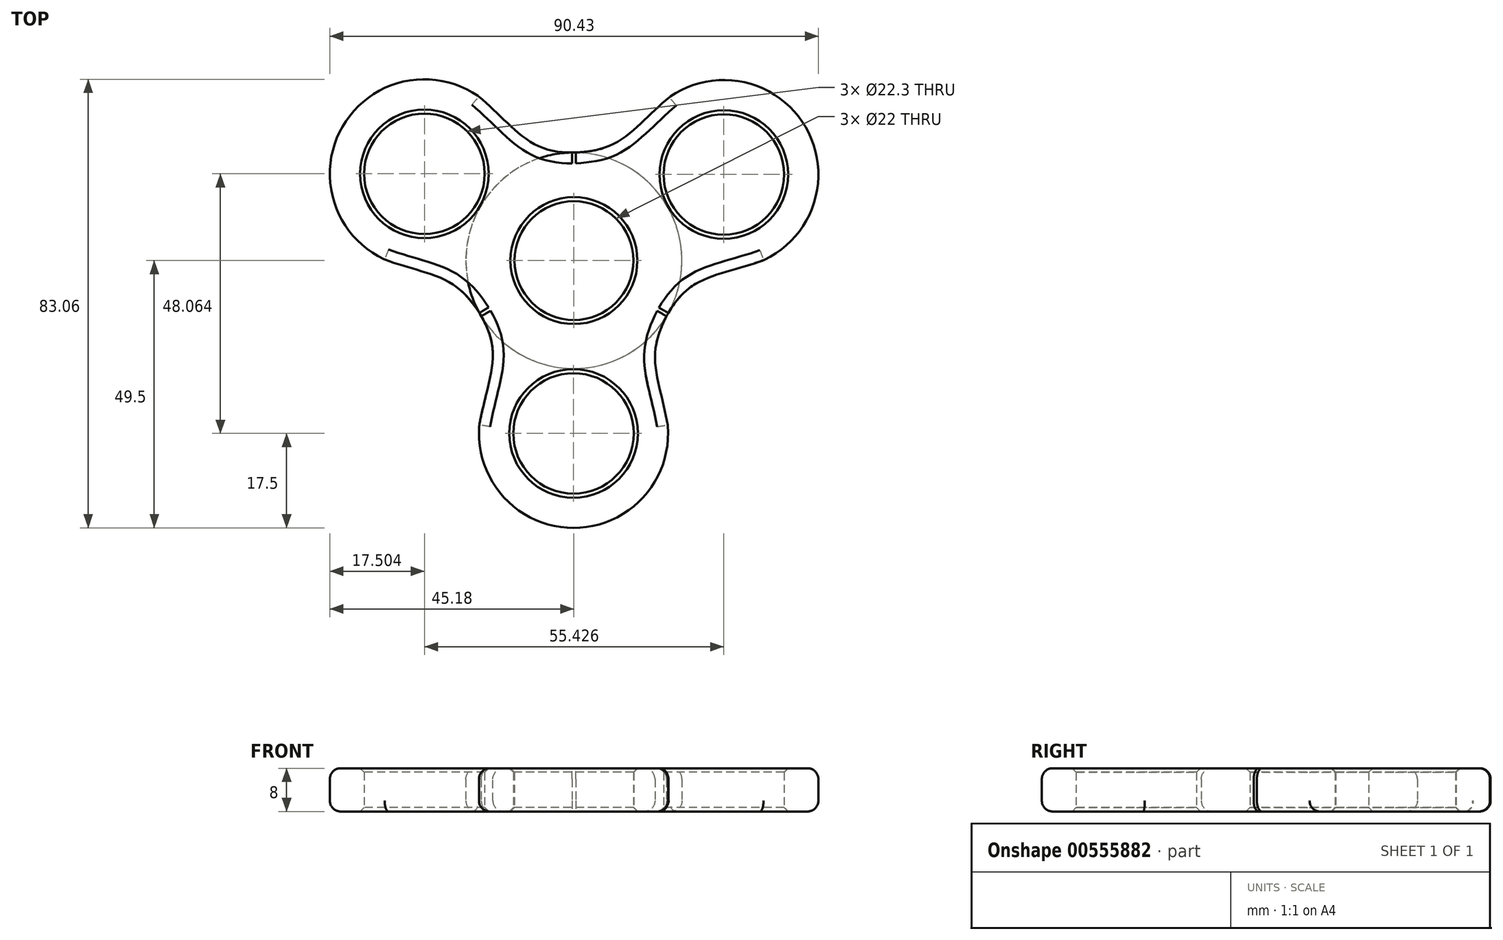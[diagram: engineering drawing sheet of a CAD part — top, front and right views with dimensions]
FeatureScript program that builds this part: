
annotation { "Feature Type Name" : "Feature", "Feature Type Description" : "" }
export const myFeature = defineFeature(function(context is Context, id is Id, definition is map)
    precondition{}
    {
        {
            var Q0;
            Q0=qCreatedBy(makeId("Top.planeOp"),FACE);
            var sketch = newSketch(context, id + "F0", { "sketchPlane" : qUnion([Q0])});
            skCircle(sketch, "E0.MirrorC", {"center": v(0, 0) * mm, "radius": 11 * mm});
            skCircle(sketch, "E1", {"center": v(-0.07, -32) * mm, "radius": 11.15 * mm});
            skLineSegment(sketch, "E2", {"start": v(0, 0) * mm, "end": v(-0.12, 20) * mm});
            skArc(sketch, "E3", {"start": v(17.15, -10.3) * mm, "mid": v(0, 20) * mm, "end": v(-17.15, -10.3) * mm});
            skFitSpline(sketch, "E4", {"points": [v(-17.51, -30.52) * mm, v(-15, -17.68) * mm, v(-17.15, -10.3) * mm], "startDerivative": vector(4.17, 24.17) * mm, "endDerivative": vector(-9.07, 15.88) * mm});
            skFitSpline(sketch, "E5", {"points": [v(17.15, -10.3) * mm, v(15, -17.68) * mm, v(17.36, -30.52) * mm], "startDerivative": vector(-7.03, -14) * mm, "endDerivative": vector(3.84, -24.18) * mm});
            skArc(sketch, "E6", {"start": v(-17.51, -30.52) * mm, "mid": v(-0.07, -49.5) * mm, "end": v(17.36, -30.52) * mm});
            skSolve(sketch);
        }
        {
            var Q0;
            Q0 = qSketchRegion(id + "F0", true);
            extrude(context, id + "F1", {"entities" : qUnion([Q0]), "depth" : 8 * mm, "offsetDistance" : 25 * mm});
        }
        {
            var Q0;
            Q0=qCreatedBy(makeId("Front.planeOp"),FACE);
            var sketch = newSketch(context, id + "F2", { "sketchPlane" : qUnion([Q0])});
            skLineSegment(sketch, "E7", {"start": v(0, 0) * mm, "end": v(0, 36.14) * mm});
            skSolve(sketch);
        }
        {
            var Q0;
            Q0=makeQuery(id+"F1.opExtrude","SWEPT_BODY",BODY,{"disambiguationData":[OSD([sQuery(id+"F0.wireOp",EDGE,"f3960193-eab3-4b8b-a0f2-21ab98192fe2"),sQuery(id+"F0.wireOp",EDGE,"da26f408-d12f-4fae-93dc-3efbcd1e3af21.MirrorC"),sQuery(id+"F0.wireOp",EDGE,"14506032-b490-4246-af5a-1439987a0185.MirrorC"),sQuery(id+"F0.wireOp",EDGE,"61171388-bded-4786-97b8-63b4edcb6984.MirrorC"),sQuery(id+"F0.wireOp",EDGE,"9475da3a-7f2b-4840-8aec-7bdfa3fc84fe.MirrorC"),sQuery(id+"F0.wireOp",EDGE,"f5e62fb9-18b1-4003-8d50-6765dd313fea"),sQuery(id+"F0.wireOp",EDGE,"e2af428d-a368-4ff8-af57-03d4f12e0fbb")])]});
            var Q1;
            Q1=makeQuery(id+"F1.opExtrude","SWEPT_BODY",BODY,{"disambiguationData":[OSD([sQuery(id+"F0.wireOp",EDGE,"E0.MirrorC"),sQuery(id+"F0.wireOp",EDGE,"E1"),sQuery(id+"F0.wireOp",EDGE,"E3"),sQuery(id+"F0.wireOp",EDGE,"E4"),sQuery(id+"F0.wireOp",EDGE,"E5"),sQuery(id+"F0.wireOp",EDGE,"E6")])]});
            var Q2;
            Q2=sQuery(id+"F2.wireOp",EDGE,"E7");
            circularPattern(context, id + "F3", {"entities" : qUnion([Q0, Q1]), "axis" : qUnion([Q2]), "angle" : 360 * degree, "instanceCount" : 3, "equalSpace" : true});
        }
        {
            var Q0;
            Q0=makeQuery(id+"F3.opPattern","COPY",EDGE,{"derivedFrom":makeQuery(id+"F1.opExtrude","CAP_EDGE",EDGE,{"disambiguationData":[OSD([sQuery(id+"F0.wireOp",EDGE,"E1")])],"isStart":false}),"instanceName":"1"});
            var Q1;
            Q1=makeQuery(id+"F3.opPattern","COPY",EDGE,{"derivedFrom":makeQuery(id+"F1.opExtrude","CAP_EDGE",EDGE,{"disambiguationData":[OSD([sQuery(id+"F0.wireOp",EDGE,"E1")])],"isStart":true}),"instanceName":"1"});
            var Q2;
            Q2=makeQuery(id+"F1.opExtrude","CAP_EDGE",EDGE,{"disambiguationData":[OSD([sQuery(id+"F0.wireOp",EDGE,"E1")])],"isStart":false});
            var Q3;
            Q3=makeQuery(id+"F1.opExtrude","CAP_EDGE",EDGE,{"disambiguationData":[OSD([sQuery(id+"F0.wireOp",EDGE,"E1")])],"isStart":true});
            var Q4;
            Q4=makeQuery(id+"F3.opPattern","COPY",EDGE,{"derivedFrom":makeQuery(id+"F1.opExtrude","CAP_EDGE",EDGE,{"disambiguationData":[OSD([sQuery(id+"F0.wireOp",EDGE,"E1")])],"isStart":false}),"instanceName":"2"});
            var Q5;
            Q5=makeQuery(id+"F3.opPattern","COPY",EDGE,{"derivedFrom":makeQuery(id+"F1.opExtrude","CAP_EDGE",EDGE,{"disambiguationData":[OSD([sQuery(id+"F0.wireOp",EDGE,"E1")])],"isStart":true}),"instanceName":"2"});
            var Q6;
            Q6=makeQuery(id+"F3.opPattern","COPY",EDGE,{"derivedFrom":makeQuery(id+"F1.opExtrude","CAP_EDGE",EDGE,{"disambiguationData":[OSD([sQuery(id+"F0.wireOp",EDGE,"61171388-bded-4786-97b8-63b4edcb6984.MirrorC")])],"isStart":false}),"instanceName":"2"});
            var Q7;
            Q7=makeQuery(id+"F3.opPattern","COPY",EDGE,{"derivedFrom":makeQuery(id+"F1.opExtrude","CAP_EDGE",EDGE,{"disambiguationData":[OSD([sQuery(id+"F0.wireOp",EDGE,"61171388-bded-4786-97b8-63b4edcb6984.MirrorC")])],"isStart":true}),"instanceName":"2"});
            var Q8;
            Q8=makeQuery(id+"F3.opPattern","COPY",EDGE,{"derivedFrom":makeQuery(id+"F1.opExtrude","CAP_EDGE",EDGE,{"disambiguationData":[OSD([sQuery(id+"F0.wireOp",EDGE,"E0.MirrorC")])],"isStart":false}),"instanceName":"2"});
            var Q9;
            Q9=makeQuery(id+"F3.opPattern","COPY",EDGE,{"derivedFrom":makeQuery(id+"F1.opExtrude","CAP_EDGE",EDGE,{"disambiguationData":[OSD([sQuery(id+"F0.wireOp",EDGE,"E0.MirrorC")])],"isStart":true}),"instanceName":"2"});
            chamfer(context, id + "F4", {"entities" : qUnion([Q0, Q1, Q2, Q3, Q4, Q5, Q6, Q7, Q8, Q9]), "width" : .75 * mm, "tangentPropagation" : true});
        }
        {
            var Q0;
            Q0=makeQuery(id+"F3.opPattern","COPY",EDGE,{"derivedFrom":makeQuery(id+"F1.opExtrude","CAP_EDGE",EDGE,{"disambiguationData":[OSD([sQuery(id+"F0.wireOp",EDGE,"E5")])],"isStart":false}),"instanceName":"2"});
            var Q1;
            Q1=makeQuery(id+"F3.opPattern","COPY",EDGE,{"derivedFrom":makeQuery(id+"F1.opExtrude","CAP_EDGE",EDGE,{"disambiguationData":[OSD([sQuery(id+"F0.wireOp",EDGE,"E6")])],"isStart":false}),"instanceName":"2"});
            var Q2;
            Q2=makeQuery(id+"F3.opPattern","COPY",EDGE,{"derivedFrom":makeQuery(id+"F1.opExtrude","CAP_EDGE",EDGE,{"disambiguationData":[OSD([sQuery(id+"F0.wireOp",EDGE,"E4")])],"isStart":false}),"instanceName":"2"});
            var Q3;
            Q3=makeQuery(id+"F1.opExtrude","CAP_EDGE",EDGE,{"disambiguationData":[OSD([sQuery(id+"F0.wireOp",EDGE,"E4")])],"isStart":false});
            var Q4;
            Q4=makeQuery(id+"F1.opExtrude","CAP_EDGE",EDGE,{"disambiguationData":[OSD([sQuery(id+"F0.wireOp",EDGE,"E6")])],"isStart":false});
            var Q5;
            Q5=makeQuery(id+"F1.opExtrude","CAP_EDGE",EDGE,{"disambiguationData":[OSD([sQuery(id+"F0.wireOp",EDGE,"E5")])],"isStart":false});
            var Q6;
            Q6=makeQuery(id+"F3.opPattern","COPY",EDGE,{"derivedFrom":makeQuery(id+"F1.opExtrude","CAP_EDGE",EDGE,{"disambiguationData":[OSD([sQuery(id+"F0.wireOp",EDGE,"E5")])],"isStart":false}),"instanceName":"1"});
            var Q7;
            Q7=makeQuery(id+"F3.opPattern","COPY",EDGE,{"derivedFrom":makeQuery(id+"F1.opExtrude","CAP_EDGE",EDGE,{"disambiguationData":[OSD([sQuery(id+"F0.wireOp",EDGE,"E6")])],"isStart":false}),"instanceName":"1"});
            var Q8;
            Q8=makeQuery(id+"F3.opPattern","COPY",EDGE,{"derivedFrom":makeQuery(id+"F1.opExtrude","CAP_EDGE",EDGE,{"disambiguationData":[OSD([sQuery(id+"F0.wireOp",EDGE,"E4")])],"isStart":false}),"instanceName":"1"});
            var Q9;
            Q9=makeQuery(id+"F3.opPattern","COPY",EDGE,{"derivedFrom":makeQuery(id+"F1.opExtrude","CAP_EDGE",EDGE,{"disambiguationData":[OSD([sQuery(id+"F0.wireOp",EDGE,"E3")])],"isStart":false}),"instanceName":"1"});
            var Q10;
            Q10=makeQuery(id+"F3.opPattern","COPY",EDGE,{"derivedFrom":makeQuery(id+"F1.opExtrude","CAP_EDGE",EDGE,{"disambiguationData":[OSD([sQuery(id+"F0.wireOp",EDGE,"E3")])],"isStart":false}),"instanceName":"2"});
            var Q11;
            Q11=makeQuery(id+"F3.opPattern","COPY",EDGE,{"derivedFrom":makeQuery(id+"F1.opExtrude","CAP_EDGE",EDGE,{"disambiguationData":[OSD([sQuery(id+"F0.wireOp",EDGE,"E3")])],"isStart":true}),"instanceName":"2"});
            var Q12;
            Q12=makeQuery(id+"F3.opPattern","COPY",EDGE,{"derivedFrom":makeQuery(id+"F1.opExtrude","CAP_EDGE",EDGE,{"disambiguationData":[OSD([sQuery(id+"F0.wireOp",EDGE,"E3")])],"isStart":true}),"instanceName":"1"});
            var Q13;
            Q13=makeQuery(id+"F1.opExtrude","CAP_EDGE",EDGE,{"disambiguationData":[OSD([sQuery(id+"F0.wireOp",EDGE,"E3")])],"isStart":true});
            var Q14;
            Q14=makeQuery(id+"F1.opExtrude","CAP_EDGE",EDGE,{"disambiguationData":[OSD([sQuery(id+"F0.wireOp",EDGE,"E3")])],"isStart":false});
            fillet(context, id + "F5", {"entities" : qUnion([Q0, Q1, Q2, Q3, Q4, Q5, Q6, Q7, Q8, Q9, Q10, Q11, Q12, Q13, Q14]), "radius" : 2 * mm, "tangentPropagation" : true, "allowEdgeOverflow" : false});
        }
        {
            var Q0;
            Q0=makeQuery(id+"F3.opPattern","COPY",EDGE,{"derivedFrom":makeQuery(id+"F1.opExtrude","CAP_EDGE",EDGE,{"disambiguationData":[OSD([sQuery(id+"F0.wireOp",EDGE,"E0.MirrorC")])],"isStart":false}),"instanceName":"1"});
            var Q1;
            Q1=makeQuery(id+"F3.opPattern","COPY",EDGE,{"derivedFrom":makeQuery(id+"F1.opExtrude","CAP_EDGE",EDGE,{"disambiguationData":[OSD([sQuery(id+"F0.wireOp",EDGE,"E0.MirrorC")])],"isStart":true}),"instanceName":"1"});
            chamfer(context, id + "F6", {"entities" : qUnion([Q0, Q1]), "width" : .75 * mm, "tangentPropagation" : true});
        }
        {
            var Q0;
            Q0=makeQuery(id+"F1.opExtrude","CAP_EDGE",EDGE,{"disambiguationData":[OSD([sQuery(id+"F0.wireOp",EDGE,"E0.MirrorC")])],"isStart":false});
            var Q1;
            Q1=makeQuery(id+"F1.opExtrude","CAP_EDGE",EDGE,{"disambiguationData":[OSD([sQuery(id+"F0.wireOp",EDGE,"E0.MirrorC")])],"isStart":true});
            chamfer(context, id + "F7", {"entities" : qUnion([Q0, Q1]), "width" : .75 * mm, "tangentPropagation" : true});
        }
        {
            var Q0;
            Q0=makeQuery(id+"F3.opPattern","COPY",EDGE,{"derivedFrom":makeQuery(id+"F1.opExtrude","CAP_EDGE",EDGE,{"disambiguationData":[OSD([sQuery(id+"F0.wireOp",EDGE,"E4")])],"isStart":true}),"instanceName":"1"});
            var Q1;
            Q1=makeQuery(id+"F1.opExtrude","CAP_EDGE",EDGE,{"disambiguationData":[OSD([sQuery(id+"F0.wireOp",EDGE,"E5")])],"isStart":true});
            var Q2;
            Q2=makeQuery(id+"F1.opExtrude","CAP_EDGE",EDGE,{"disambiguationData":[OSD([sQuery(id+"F0.wireOp",EDGE,"E6")])],"isStart":true});
            var Q3;
            Q3=makeQuery(id+"F1.opExtrude","CAP_EDGE",EDGE,{"disambiguationData":[OSD([sQuery(id+"F0.wireOp",EDGE,"E4")])],"isStart":true});
            var Q4;
            Q4=makeQuery(id+"F3.opPattern","COPY",EDGE,{"derivedFrom":makeQuery(id+"F1.opExtrude","CAP_EDGE",EDGE,{"disambiguationData":[OSD([sQuery(id+"F0.wireOp",EDGE,"E5")])],"isStart":true}),"instanceName":"2"});
            var Q5;
            Q5=makeQuery(id+"F3.opPattern","COPY",EDGE,{"derivedFrom":makeQuery(id+"F1.opExtrude","CAP_EDGE",EDGE,{"disambiguationData":[OSD([sQuery(id+"F0.wireOp",EDGE,"E6")])],"isStart":true}),"instanceName":"2"});
            var Q6;
            Q6=makeQuery(id+"F3.opPattern","COPY",EDGE,{"derivedFrom":makeQuery(id+"F1.opExtrude","CAP_EDGE",EDGE,{"disambiguationData":[OSD([sQuery(id+"F0.wireOp",EDGE,"E4")])],"isStart":true}),"instanceName":"2"});
            var Q7;
            Q7=makeQuery(id+"F3.opPattern","COPY",EDGE,{"derivedFrom":makeQuery(id+"F1.opExtrude","CAP_EDGE",EDGE,{"disambiguationData":[OSD([sQuery(id+"F0.wireOp",EDGE,"E5")])],"isStart":true}),"instanceName":"1"});
            var Q8;
            Q8=makeQuery(id+"F3.opPattern","COPY",EDGE,{"derivedFrom":makeQuery(id+"F1.opExtrude","CAP_EDGE",EDGE,{"disambiguationData":[OSD([sQuery(id+"F0.wireOp",EDGE,"E6")])],"isStart":true}),"instanceName":"1"});
            fillet(context, id + "F8", {"entities" : qUnion([Q0, Q1, Q2, Q3, Q4, Q5, Q6, Q7, Q8]), "radius" : 2 * mm, "tangentPropagation" : true, "allowEdgeOverflow" : false});
        }
    });
